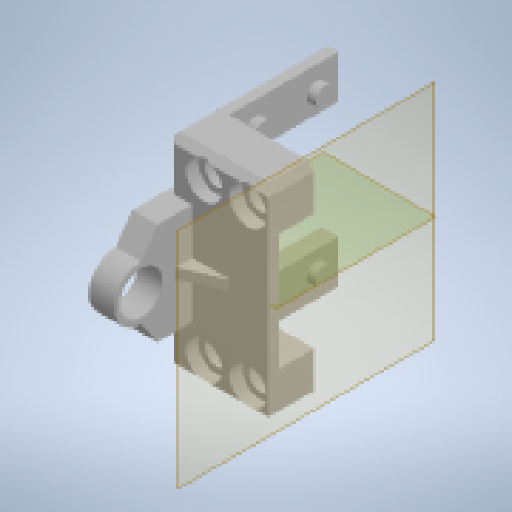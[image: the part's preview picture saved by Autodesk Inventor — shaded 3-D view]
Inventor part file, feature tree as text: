
AUTODESK INVENTOR PART (.ipt)
format: ipt  version: 2023 (Build 270158000, 158)  size: 307,200 bytes
history: native  units: mm
features: reference x14, extrude x8, sketch x8, other x7, plane x3, projected_geometry x2, mirror x1, chamfer x1
ambient origin geometry x8: Origin, YZ Plane, XZ Plane, XY Plane, X Axis, Y Axis, Z Axis, Center Point
bodies: Solid1 (feature_tree)
feature tree (44):
  plane  "Work Plane2"
  extrude  "Extrusion1"  Depth=0.5mm
  extrude  "Extrusion2"  Depth=10.0mm
  extrude  "Extrusion3"  Depth=2.5mm TaperAngle=0.0deg
  other  "Work Point2"
  other  "Work Point1"
  plane  "Work Plane1"
  mirror  "Mirror1"
  extrude  "Extrusion4"  Depth=3.0mm
  plane  "Work Plane3"
  extrude  "Extrusion5"  Depth=7.5mm TaperAngle=0.0deg
  extrude  "Extrusion6"  Depth=3.75mm
  chamfer  "Chamfer2"  Distance=3.75mm
  extrude  "Extrusion9"  Depth=7.0mm
  extrude  "Extrusion10"  Depth=15.0mm
  sketch  "Sketch1"  dims[d0=0.25mm d1=0.5mm]
  reference  "Reference1"
  reference  "Reference2"
  reference  "Reference3"
  sketch  "Sketch2"  dims[d2=10.0mm d3=0.0mm d4=0.3mm]
  reference  "Reference4"
  sketch  "Sketch3"  dims[d5=5.0mm d6=0.0mm d8=2.5mm d9=0.0mm]
  sketch  "Sketch5"  dims[d11=3.0mm d12=0.0mm d13=16.0mm]
  sketch  "Sketch6"  dims[d15=12.5mm d17=7.5mm d18=0.0mm]
  sketch  "Sketch7"  dims[d19=25.25mm d20=0.0mm d21=1.5mm d22=3.75mm d23=0.0mm]
  reference  "Reference11"
  reference  "Reference12"
  reference  "Reference13"
  reference  "Reference14"
  sketch  "Sketch10"  dims[d35=2.0mm d36=2.0mm d37=45.0deg d38=7.0mm]
  reference  "Reference15"
  reference  "Reference16"
  reference  "Reference17"
  reference  "Reference18"
  sketch  "Sketch12"  dims[d39=28.0mm d40=0.0mm d41=15.0mm d42=30.0mm d43=5.0mm d44=3.0mm d45=0.0mm d46=0.25mm d47=0.25mm d48=5.6mm]
  projected_geometry  "Projected Loop7"
  projected_geometry  "Projected Loop8"
  reference  "Reference19"
  reference  "Reference20"
  other  "<userpath> laptop\Desktop\CNC_Project\X_GANTRY.iam"
  other  "X_GANTRY.iam"
  other  "BK12:1"
  other  "BK12_Spacer:1"
  other  "<userpath>\OneDrive\Desktop\CNC_Project\X_GANTRY.iam"
